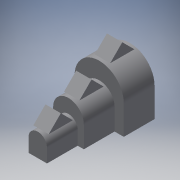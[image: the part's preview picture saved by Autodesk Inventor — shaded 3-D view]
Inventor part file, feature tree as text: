
AUTODESK INVENTOR PART (.ipt)
format: ipt  version: 2016 (Build 200138000, 138)  size: 202,752 bytes
history: native  units: in
note: dims shown in document units (in); Inventor stores cm internally (conversion verified against a paired STEP export)
features: extrude x10, sketch x10, reference x4, plane x1, projected_geometry x1
ambient origin geometry x8: Origin, YZ Plane, XZ Plane, XY Plane, X Axis, Y Axis, Z Axis, Center Point
bodies: Solid1 (feature_tree)
feature tree (26):
  extrude  "Extrusion1"  Depth=0.197in
  extrude  "Extrusion2"  Depth=0.4in
  extrude  "Extrusion3"  Depth=0.4in TaperAngle=0.0deg
  extrude  "Extrusion4"  Depth=1.0in TaperAngle=0.0deg
  extrude  "Extrusion5"  Depth=1.6in
  plane  "Work Plane1"
  extrude  "Extrusion8"  Depth=1.0in
  extrude  "Extrusion9"  Depth=0.6in
  extrude  "Extrusion10"  Depth=0.1065in
  extrude  "Extrusion11"  Depth=0.394in
  extrude  "Extrusion12"  Depth=0.5in TaperAngle=0.0deg
  sketch  "Sketch1"  dims[d1=1.0in d2=0.0in d3=0.197in]
  reference  "Reference1"
  sketch  "Sketch2"  dims[d4=0.4in d5=0.0in d6=0.15in]
  reference  "Reference2"
  sketch  "Sketch3"  dims[d7=0.1772in d8=0.4in d9=0.0in]
  sketch  "Sketch4"  dims[d11=1.0in d12=0.0in d15=1.0in d16=0.0in]
  sketch  "Sketch5"  dims[d25=0.75in d26=1.6in]
  sketch  "Sketch8"  dims[d27=0.25in d28=1.0in]
  sketch  "Sketch9"  dims[d29=0.25in d30=0.6in]
  sketch  "Sketch10"  dims[d31=-0.8in d32=0.1065in]
  sketch  "Sketch11"  dims[d33=0.787in d34=0.394in]
  projected_geometry  "Projected Loop1"
  sketch  "Sketch12"  dims[d35=0.394in d36=0.5in d37=0.0in d38=0.1065in d39=0.787in d40=0.394in d41=0.394in d42=0.5in d43=0.0in d44=0.1065in d45=0.787in d46=0.394in d47=0.394in d48=0.5in d49=0.0in d50=0.0079in d51=0.0in d52=0.0394in d53=0.0394in d54=0.098in d55=0.098in d56=1.0in d57=0.0in]
  reference  "Reference3"
  reference  "Reference4"
